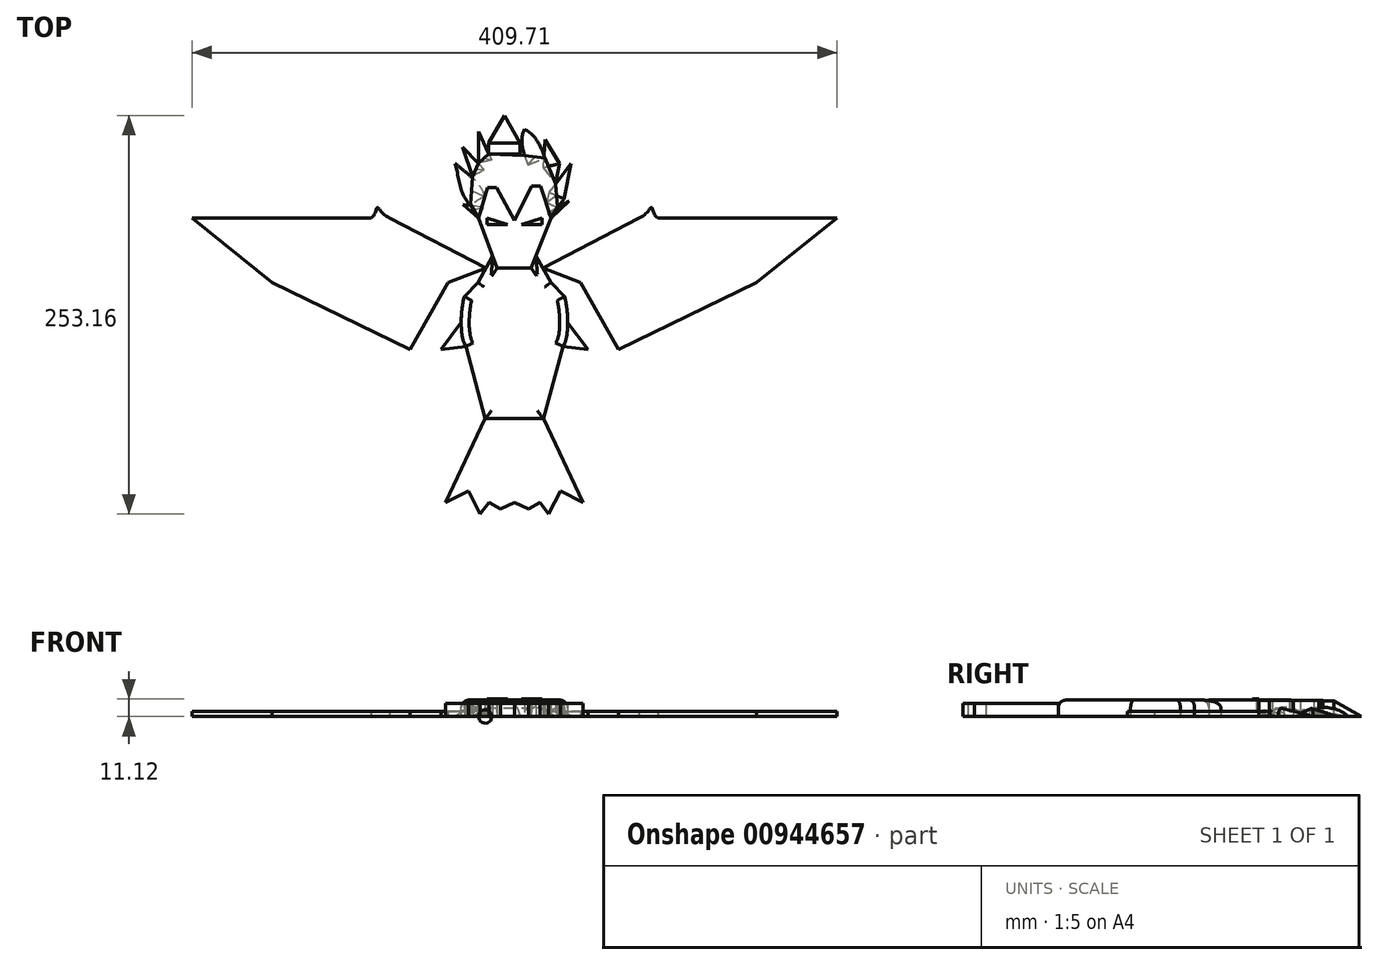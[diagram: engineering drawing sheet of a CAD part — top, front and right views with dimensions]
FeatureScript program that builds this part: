
annotation { "Feature Type Name" : "Feature", "Feature Type Description" : "" }
export const myFeature = defineFeature(function(context is Context, id is Id, definition is map)
    precondition{}
    {
        {
            var Q0;
            Q0=qCreatedBy(makeId("Top.planeOp"),FACE);
            var sketch = newSketch(context, id + "F0", { "sketchPlane" : qUnion([Q0])});
            skLineSegment(sketch, "E0", {"start": v(-66.9, 0) * mm, "end": v(-76.6, 8.61) * mm});
            skLineSegment(sketch, "E1", {"start": v(-76.6, 8.61) * mm, "end": v(-71.81, 8.61) * mm});
            skFitSpline(sketch, "E2", {"points": [v(-71.81, 8.61) * mm, v(-81.52, 34.84) * mm], "startDerivative": vector(-20.15, 14.33) * mm, "endDerivative": vector(-6.58, 25.07) * mm});
            skLineSegment(sketch, "E3", {"start": v(-81.52, 34.84) * mm, "end": v(-70.5, 26.48) * mm});
            skPoint(sketch, "E4.endSnap0", {"position": v(-76.81, 45.33) * mm});
            skLineSegment(sketch, "E5", {"start": v(-66.7, 55.01) * mm, "end": v(-60.24, 40.68) * mm});
            skLineSegment(sketch, "E6", {"start": v(-60.24, 40.68) * mm, "end": v(-60.24, 47.85) * mm});
            skPoint(sketch, "E6.endSnap0", {"position": v(-63.47, 47.85) * mm});
            skLineSegment(sketch, "E7", {"start": v(-60.24, 47.85) * mm, "end": v(-50.37, 65.3) * mm});
            skLineSegment(sketch, "E8", {"start": v(-50.37, 65.3) * mm, "end": v(-45.15, 49.34) * mm});
            skFitSpline(sketch, "E9", {"points": [v(-45.15, 49.34) * mm, v(-37.68, 39.91) * mm], "startDerivative": vector(4.86, -11.5) * mm, "endDerivative": vector(8.7, -8.59) * mm});
            skLineSegment(sketch, "E10", {"start": v(-37.68, 39.91) * mm, "end": v(-37.68, 56.57) * mm});
            skPoint(sketch, "E10.endSnap0", {"position": v(-55.3, 56.57) * mm});
            skFitSpline(sketch, "E11", {"points": [v(-37.68, 56.57) * mm, v(-24.45, 38.08) * mm], "startDerivative": vector(23.87, -11.8) * mm, "endDerivative": vector(8.76, -22.04) * mm});
            skLineSegment(sketch, "E12", {"start": v(-24.45, 38.08) * mm, "end": v(-24.45, 49.93) * mm});
            skLineSegment(sketch, "E13", {"start": v(-24.45, 49.93) * mm, "end": v(-15.46, 34.62) * mm});
            skLineSegment(sketch, "E14", {"start": v(-15.46, 34.62) * mm, "end": v(-17.97, 22.12) * mm});
            skLineSegment(sketch, "E15", {"start": v(-17.97, 22.12) * mm, "end": v(-8.1, 34.62) * mm});
            skLineSegment(sketch, "E16", {"start": v(-8.1, 34.62) * mm, "end": v(-12.58, 12.28) * mm});
            skLineSegment(sketch, "E17", {"start": v(-12.58, 12.28) * mm, "end": v(-16.62, 6.75) * mm});
            skLineSegment(sketch, "E18", {"start": v(-70.5, 26.48) * mm, "end": v(-76.81, 45.33) * mm});
            skLineSegment(sketch, "E19", {"start": v(-66.7, 55.01) * mm, "end": v(-66.7, 35.15) * mm});
            skLineSegment(sketch, "E20", {"start": v(-66.7, 35.15) * mm, "end": v(-76.81, 45.33) * mm});
            skPoint(sketch, "E21.endSnap0", {"position": v(-73.65, 35.9) * mm});
            skLineSegment(sketch, "E22", {"start": v(-43.94, -1.42) * mm, "end": v(-55.3, 19.57) * mm});
            skLineSegment(sketch, "E23", {"start": v(-43.94, -1.42) * mm, "end": v(-33, 20.48) * mm});
            skLineSegment(sketch, "E24", {"start": v(-55.3, 19.57) * mm, "end": v(-60.93, 19.57) * mm});
            skLineSegment(sketch, "E25", {"start": v(-60.93, 19.57) * mm, "end": v(-66.9, 0) * mm});
            skLineSegment(sketch, "E26", {"start": v(-33, 20.48) * mm, "end": v(-27.37, 20.48) * mm});
            skLineSegment(sketch, "E27", {"start": v(-27.37, 20.48) * mm, "end": v(-21.96, 3.92) * mm});
            skLineSegment(sketch, "E28", {"start": v(-21.96, 3.92) * mm, "end": v(-20.68, 0) * mm});
            skLineSegment(sketch, "E29", {"start": v(-16.62, 6.75) * mm, "end": v(-9.22, 10.96) * mm});
            skLineSegment(sketch, "E30", {"start": v(-9.22, 10.96) * mm, "end": v(-20.68, 0) * mm});
            skLineSegment(sketch, "E31", {"start": v(-66.9, 0) * mm, "end": v(-54.89, -31.63) * mm});
            skLineSegment(sketch, "E32", {"start": v(-54.89, -31.63) * mm, "end": v(-43.94, -31.63) * mm});
            skLineSegment(sketch, "E33", {"start": v(-43.94, -31.63) * mm, "end": v(-33.27, -31.63) * mm});
            skLineSegment(sketch, "E34", {"start": v(-33.27, -31.63) * mm, "end": v(-20.68, 0) * mm});
            skLineSegment(sketch, "E35", {"start": v(-43.94, -1.42) * mm, "end": v(-43.94, -31.63) * mm, "construction": true});
            skLineSegment(sketch, "E36", {"start": v(-64.46, -6.43) * mm, "end": v(-22.05, -6.43) * mm, "construction": true});
            skLineSegment(sketch, "E37", {"start": v(-43.94, -1.42) * mm, "end": v(-43.94, 31.12) * mm, "construction": true});
            skLineSegment(sketch, "E38", {"start": v(-30.23, -24) * mm, "end": v(-20.68, -40.76) * mm});
            skLineSegment(sketch, "E39.MirrorCS", {"start": v(-57.66, -24) * mm, "end": v(-64.77, -36.48) * mm});
            skLineSegment(sketch, "E40", {"start": v(-62, -31.63) * mm, "end": v(-74.02, -36.2) * mm});
            skLineSegment(sketch, "E41.MirrorCS", {"start": v(-25.88, -31.63) * mm, "end": v(-1.86, -40.76) * mm});
            skLineSegment(sketch, "E42", {"start": v(-86.03, -40.76) * mm, "end": v(-111.7, -86.16) * mm});
            skLineSegment(sketch, "E43", {"start": v(-43.94, -31.63) * mm, "end": v(-43.94, -131.11) * mm, "construction": true});
            skLineSegment(sketch, "E44.MirrorCS", {"start": v(-1.86, -40.76) * mm, "end": v(37.93, -111.15) * mm});
            skPoint(sketch, "E45.startSnap0", {"position": v(-43.94, -81.37) * mm});
            skLineSegment(sketch, "E46", {"start": v(-43.94, -81.37) * mm, "end": v(-13.98, -81.37) * mm, "construction": true});
            skLineSegment(sketch, "E47", {"start": v(-43.94, -81.37) * mm, "end": v(-74.8, -81.37) * mm, "construction": true});
            skFitSpline(sketch, "E48", {"points": [v(-75.76, -49.7) * mm, v(-74.8, -81.37) * mm], "startDerivative": vector(-6.65, -23.76) * mm, "endDerivative": vector(13.3, -20.9) * mm});
            skFitSpline(sketch, "E49.MirrorCS", {"points": [v(-12.13, -49.7) * mm, v(-13.08, -81.37) * mm], "startDerivative": vector(6.65, -23.76) * mm, "endDerivative": vector(-13.3, -20.9) * mm});
            skLineSegment(sketch, "E50", {"start": v(-74.8, -81.37) * mm, "end": v(-62.45, -127.34) * mm});
            skLineSegment(sketch, "E51.MirrorCS", {"start": v(-13.08, -81.37) * mm, "end": v(-25.43, -127.34) * mm});
            skLineSegment(sketch, "E52", {"start": v(-77.78, -66.16) * mm, "end": v(-115.4, -116.45) * mm});
            skLineSegment(sketch, "E53.MirrorCS", {"start": v(-10.1, -66.16) * mm, "end": v(27.52, -116.45) * mm});
            skLineSegment(sketch, "E54", {"start": v(-49.42, -31.63) * mm, "end": v(-46.5, -45.27) * mm});
            skLineSegment(sketch, "E55.MirrorCS", {"start": v(-38.47, -31.63) * mm, "end": v(-41.39, -45.27) * mm});
            skLineSegment(sketch, "E56", {"start": v(-62.45, -127.34) * mm, "end": v(-25.43, -127.34) * mm});
            skLineSegment(sketch, "E57", {"start": v(-62.45, -127.34) * mm, "end": v(-87.56, -180.45) * mm});
            skLineSegment(sketch, "E58", {"start": v(-43.94, -131.11) * mm, "end": v(-43.94, -225.81) * mm, "construction": true});
            skLineSegment(sketch, "E59", {"start": v(-87.56, -180.45) * mm, "end": v(-73.11, -173.13) * mm});
            skLineSegment(sketch, "E60", {"start": v(-73.11, -173.13) * mm, "end": v(-65.65, -187.87) * mm});
            skLineSegment(sketch, "E61", {"start": v(-65.65, -187.87) * mm, "end": v(-60.1, -180.45) * mm});
            skLineSegment(sketch, "E62", {"start": v(-60.1, -180.45) * mm, "end": v(-52.85, -184.55) * mm});
            skLineSegment(sketch, "E63", {"start": v(-52.85, -184.55) * mm, "end": v(-43.94, -180.45) * mm});
            skLineSegment(sketch, "E64.MirrorCS", {"start": v(-25.43, -127.34) * mm, "end": v(-0.32, -180.45) * mm});
            skLineSegment(sketch, "E65.MirrorCS", {"start": v(-0.32, -180.45) * mm, "end": v(-14.77, -173.13) * mm});
            skLineSegment(sketch, "E66.MirrorCS", {"start": v(-14.77, -173.13) * mm, "end": v(-22.24, -187.87) * mm});
            skLineSegment(sketch, "E67.MirrorCS", {"start": v(-27.8, -180.45) * mm, "end": v(-35.04, -184.55) * mm});
            skLineSegment(sketch, "E68.MirrorCS", {"start": v(-35.04, -184.55) * mm, "end": v(-43.94, -180.45) * mm});
            skLineSegment(sketch, "E69.MirrorCS", {"start": v(-22.24, -187.87) * mm, "end": v(-27.8, -180.45) * mm});
            skPoint(sketch, "E70.1.internal.snap0", {"position": v(-69.38, -180.5) * mm});
            skLineSegment(sketch, "E71", {"start": v(-73.11, -173.13) * mm, "end": v(-113.4, -264.9) * mm});
            skLineSegment(sketch, "E72.MirrorCS", {"start": v(-14.77, -173.13) * mm, "end": v(25.5, -264.9) * mm});
            skLineSegment(sketch, "E73", {"start": v(-35.04, -184.55) * mm, "end": v(9.92, -264.08) * mm});
            skLineSegment(sketch, "E74.MirrorCS", {"start": v(-52.85, -184.55) * mm, "end": v(-97.8, -264.08) * mm});
            skLineSegment(sketch, "E75", {"start": v(-67.2, -40.76) * mm, "end": v(-71.48, -45.22) * mm});
            skLineSegment(sketch, "E76", {"start": v(-20.68, -40.76) * mm, "end": v(-12.13, -49.7) * mm});
            skLineSegment(sketch, "E77", {"start": v(-125.82, -111.15) * mm, "end": v(-115.4, -116.45) * mm});
            skLineSegment(sketch, "E78", {"start": v(27.52, -116.45) * mm, "end": v(37.93, -111.15) * mm});
            skLineSegment(sketch, "E79", {"start": v(9.92, -264.08) * mm, "end": v(25.5, -264.9) * mm});
            skLineSegment(sketch, "E80", {"start": v(-113.4, -264.9) * mm, "end": v(-97.8, -264.08) * mm});
            skLineSegment(sketch, "E81", {"start": v(-115.4, -116.45) * mm, "end": v(-115.4, -116.45) * mm});
            skLineSegment(sketch, "E82", {"start": v(-111.7, -86.16) * mm, "end": v(-125.82, -111.15) * mm});
            skLineSegment(sketch, "E83", {"start": v(-74.02, -36.2) * mm, "end": v(-86.03, -40.76) * mm});
            skLineSegment(sketch, "E84", {"start": v(-71.48, -45.22) * mm, "end": v(-75.76, -49.7) * mm});
            skLineSegment(sketch, "E85", {"start": v(-64.77, -36.48) * mm, "end": v(-67.2, -40.76) * mm});
            skLineSegment(sketch, "E86", {"start": v(-37.68, 39.91) * mm, "end": v(-24.45, 38.08) * mm});
            skLineSegment(sketch, "E87", {"start": v(-24.45, 38.08) * mm, "end": v(-17.97, 22.12) * mm});
            skLineSegment(sketch, "E88", {"start": v(-17.97, 22.12) * mm, "end": v(-16.62, 6.75) * mm});
            skLineSegment(sketch, "E89", {"start": v(-16.62, 6.75) * mm, "end": v(-20.68, 0) * mm});
            skLineSegment(sketch, "E90", {"start": v(-37.68, 39.91) * mm, "end": v(-60.24, 40.68) * mm});
            skLineSegment(sketch, "E91", {"start": v(-60.24, 40.68) * mm, "end": v(-66.7, 35.15) * mm});
            skLineSegment(sketch, "E92", {"start": v(-66.7, 35.15) * mm, "end": v(-70.5, 26.48) * mm});
            skLineSegment(sketch, "E93", {"start": v(-70.5, 26.48) * mm, "end": v(-71.81, 8.61) * mm});
            skLineSegment(sketch, "E94", {"start": v(-71.81, 8.61) * mm, "end": v(-66.9, 0) * mm});
            skLineSegment(sketch, "E95", {"start": v(-81.52, 34.84) * mm, "end": v(-71.15, 17.55) * mm});
            skLineSegment(sketch, "E96", {"start": v(-76.81, 45.33) * mm, "end": v(-68.4, 31.28) * mm});
            skLineSegment(sketch, "E97", {"start": v(-66.7, 55.01) * mm, "end": v(-63.02, 38.3) * mm});
            skLineSegment(sketch, "E98", {"start": v(-24.45, 49.93) * mm, "end": v(-17.97, 22.12) * mm});
            skLineSegment(sketch, "E99", {"start": v(-8.1, 34.62) * mm, "end": v(-17.3, 14.43) * mm});
            skLineSegment(sketch, "E100", {"start": v(-9.22, 10.96) * mm, "end": v(-18.07, 4.33) * mm});
            skLineSegment(sketch, "E101", {"start": v(-50.37, 65.3) * mm, "end": v(-50.37, 40.35) * mm});
            skLineSegment(sketch, "E102", {"start": v(-37.68, 56.57) * mm, "end": v(-31.07, 39) * mm});
            skLineSegment(sketch, "E103", {"start": v(-76.6, 8.61) * mm, "end": v(-70.13, 5.66) * mm});
            skLineSegment(sketch, "E104", {"start": v(-25.88, -31.63) * mm, "end": v(35.22, 0) * mm});
            skLineSegment(sketch, "E105", {"start": v(35.22, 0) * mm, "end": v(160.91, 0) * mm});
            skLineSegment(sketch, "E106", {"start": v(160.91, 0) * mm, "end": v(109.93, -40.76) * mm});
            skLineSegment(sketch, "E107.MirrorCS", {"start": v(-123.1, 0) * mm, "end": v(-248.8, 0) * mm});
            skLineSegment(sketch, "E108.MirrorCS", {"start": v(-62, -31.63) * mm, "end": v(-123.1, 0) * mm});
            skLineSegment(sketch, "E109.MirrorCS", {"start": v(-248.8, 0) * mm, "end": v(-197.82, -40.76) * mm});
            skLineSegment(sketch, "E110", {"start": v(109.93, -40.76) * mm, "end": v(22.27, -83.44) * mm});
            skLineSegment(sketch, "E111.MirrorCS", {"start": v(-197.82, -40.76) * mm, "end": v(-110.15, -83.44) * mm});
            skLineSegment(sketch, "E112", {"start": v(-90.7, -83.44) * mm, "end": v(-74.8, -81.37) * mm});
            skLineSegment(sketch, "E113.MirrorCS", {"start": v(2.82, -83.44) * mm, "end": v(-13.08, -81.37) * mm});
            skFitSpline(sketch, "E114", {"points": [v(35.22, 0) * mm, v(43.15, 6.85) * mm, v(47.2, 0) * mm], "startDerivative": vector(30.5, 14.02) * mm, "endDerivative": vector(21.86, -16.08) * mm});
            skFitSpline(sketch, "E115.MirrorCS", {"points": [v(-123.1, 0) * mm, v(-131.03, 6.85) * mm, v(-135.1, 0) * mm], "startDerivative": vector(-30.5, 14.02) * mm, "endDerivative": vector(-21.86, -16.08) * mm});
            skSolve(sketch);
        }
        {
            var Q0;
            {var subQ0=sQuery(id+"F0.wireOp",EDGE,"E2");Q0=makeQuery(id+"F0.imprint","IMPRINT",FACE,{"disambiguationData":[TD([[makeQuery(id+"F0.imprint","IMPRINT",EDGE,{"derivedFrom":subQ0}),-1.0]])]});}
            var Q1;
            Q1=sQuery(id+"F0.wireOp",EDGE,"E95");
            revolve(context, id + "F1", {"surfaceOperationType" : NewSurfaceOperationType.NEW, "entities" : qUnion([Q0]), "axis" : qUnion([Q1]), "revolveType" : RevolveType.ONE_DIRECTION, "oppositeDirection" : true, "angle" : 180 * degree});
        }
        {
            var Q0;
            {var subQ0=sQuery(id+"F0.wireOp",EDGE,"E18");Q0=makeQuery(id+"F0.imprint","IMPRINT",FACE,{"disambiguationData":[TD([[makeQuery(id+"F0.imprint","IMPRINT",EDGE,{"derivedFrom":subQ0}),-1.0]])]});}
            var Q1;
            Q1=sQuery(id+"F0.wireOp",EDGE,"E96");
            revolve(context, id + "F2", {"surfaceOperationType" : NewSurfaceOperationType.NEW, "entities" : qUnion([Q0]), "axis" : qUnion([Q1]), "revolveType" : RevolveType.ONE_DIRECTION, "oppositeDirection" : true, "angle" : 180 * degree});
        }
        {
            var Q0;
            {var subQ0=sQuery(id+"F0.wireOp",EDGE,"E19");Q0=makeQuery(id+"F0.imprint","IMPRINT",FACE,{"disambiguationData":[TD([[makeQuery(id+"F0.imprint","IMPRINT",EDGE,{"derivedFrom":subQ0}),1.0]])]});}
            var Q1;
            Q1=sQuery(id+"F0.wireOp",EDGE,"E97");
            revolve(context, id + "F3", {"surfaceOperationType" : NewSurfaceOperationType.NEW, "entities" : qUnion([Q0]), "axis" : qUnion([Q1]), "revolveType" : RevolveType.ONE_DIRECTION, "oppositeDirection" : true, "angle" : 180 * degree});
        }
        {
            var Q0;
            Q0=makeQuery(id+"F0.imprint","IMPRINT",FACE,{"disambiguationData":[TD([[makeQuery(id+"F0.imprint","IMPRINT",EDGE,{"derivedFrom":sQuery(id+"F0.wireOp",EDGE,"E13")}),-1.0]])]});
            var Q1;
            Q1=sQuery(id+"F0.wireOp",EDGE,"E98");
            revolve(context, id + "F4", {"surfaceOperationType" : NewSurfaceOperationType.NEW, "entities" : qUnion([Q0]), "axis" : qUnion([Q1]), "revolveType" : RevolveType.ONE_DIRECTION, "angle" : 180 * degree});
        }
        {
            var Q0;
            Q0=makeQuery(id+"F0.imprint","IMPRINT",FACE,{"disambiguationData":[TD([[makeQuery(id+"F0.imprint","IMPRINT",EDGE,{"derivedFrom":sQuery(id+"F0.wireOp",EDGE,"E16")}),-1.0]])]});
            var Q1;
            Q1=sQuery(id+"F0.wireOp",EDGE,"E99");
            revolve(context, id + "F5", {"surfaceOperationType" : NewSurfaceOperationType.NEW, "entities" : qUnion([Q0]), "axis" : qUnion([Q1]), "revolveType" : RevolveType.ONE_DIRECTION, "angle" : 180 * degree});
        }
        {
            var Q0;
            {var subQ0=sQuery(id+"F0.wireOp",EDGE,"E30");Q0=makeQuery(id+"F0.imprint","IMPRINT",FACE,{"disambiguationData":[TD([[makeQuery(id+"F0.imprint","IMPRINT",EDGE,{"derivedFrom":subQ0}),-1.0]])]});}
            var Q1;
            Q1=sQuery(id+"F0.wireOp",EDGE,"E100");
            revolve(context, id + "F6", {"surfaceOperationType" : NewSurfaceOperationType.NEW, "entities" : qUnion([Q0]), "axis" : qUnion([Q1]), "revolveType" : RevolveType.ONE_DIRECTION, "angle" : 180 * degree});
        }
        {
            var Q0;
            {var subQ0=sQuery(id+"F0.wireOp",EDGE,"E11");Q0=makeQuery(id+"F0.imprint","IMPRINT",FACE,{"disambiguationData":[TD([[makeQuery(id+"F0.imprint","IMPRINT",EDGE,{"derivedFrom":subQ0}),-1.0]])]});}
            var Q1;
            Q1=sQuery(id+"F0.wireOp",EDGE,"E102");
            revolve(context, id + "F7", {"operationType" : NewBodyOperationType.ADD, "surfaceOperationType" : NewSurfaceOperationType.NEW, "entities" : qUnion([Q0]), "axis" : qUnion([Q1]), "revolveType" : RevolveType.ONE_DIRECTION, "angle" : 180 * degree});
        }
        {
            var Q0;
            {var subQ0=sQuery(id+"F0.wireOp",EDGE,"E6");Q0=makeQuery(id+"F0.imprint","IMPRINT",FACE,{"disambiguationData":[TD([[makeQuery(id+"F0.imprint","IMPRINT",EDGE,{"derivedFrom":subQ0}),-1.0]])]});}
            var Q1;
            Q1=sQuery(id+"F0.wireOp",EDGE,"E101");
            revolve(context, id + "F8", {"operationType" : NewBodyOperationType.ADD, "surfaceOperationType" : NewSurfaceOperationType.NEW, "entities" : qUnion([Q0]), "axis" : qUnion([Q1]), "revolveType" : RevolveType.ONE_DIRECTION, "oppositeDirection" : true, "angle" : 180 * degree});
        }
        {
            var Q0;
            {var subQ0=sQuery(id+"F0.wireOp",EDGE,"E0");Q0=makeQuery(id+"F0.imprint","IMPRINT",FACE,{"disambiguationData":[TD([[makeQuery(id+"F0.imprint","IMPRINT",EDGE,{"derivedFrom":subQ0}),-1.0]])]});}
            var Q1;
            Q1=sQuery(id+"F0.wireOp",EDGE,"E103");
            revolve(context, id + "F9", {"surfaceOperationType" : NewSurfaceOperationType.NEW, "entities" : qUnion([Q0]), "axis" : qUnion([Q1]), "revolveType" : RevolveType.ONE_DIRECTION, "oppositeDirection" : true, "angle" : 180 * degree});
        }
        {
            var Q0;
            Q0=makeQuery(id+"F0.imprint","IMPRINT",FACE,{"disambiguationData":[TD([[makeQuery(id+"F0.imprint","IMPRINT",EDGE,{"derivedFrom":sQuery(id+"F0.wireOp",EDGE,"E22")}),-1.0]])]});
            extrude(context, id + "F10", {"entities" : qUnion([Q0]), "depth" : 10.16 * mm, "offsetDistance" : 25.4 * mm});
        }
        {
            var Q0;
            {var subQ20=sQuery(id+"F0.wireOp",EDGE,"E50");Q0=makeQuery(id+"F0.imprint","IMPRINT",FACE,{"disambiguationData":[TD([[makeQuery(id+"F0.imprint","IMPRINT",EDGE,{"derivedFrom":subQ20}),1.0]])]});}
            extrude(context, id + "F11", {"entities" : qUnion([Q0]), "depth" : 10.4 * mm, "offsetDistance" : 25.4 * mm});
        }
        {
            var Q0;
            Q0=makeQuery(id+"F11.opExtrude","CAP_FACE",FACE,{"disambiguationData":[OSD([sQuery(id+"F0.wireOp",EDGE,"E31"),sQuery(id+"F0.wireOp",EDGE,"E32"),sQuery(id+"F0.wireOp",EDGE,"E33"),sQuery(id+"F0.wireOp",EDGE,"E34"),sQuery(id+"F0.wireOp",EDGE,"E38"),sQuery(id+"F0.wireOp",EDGE,"E39.MirrorCS"),sQuery(id+"F0.wireOp",EDGE,"E48"),sQuery(id+"F0.wireOp",EDGE,"E49.MirrorCS"),sQuery(id+"F0.wireOp",EDGE,"E50"),sQuery(id+"F0.wireOp",EDGE,"E51.MirrorCS"),sQuery(id+"F0.wireOp",EDGE,"E56"),sQuery(id+"F0.wireOp",EDGE,"E75"),sQuery(id+"F0.wireOp",EDGE,"E76"),sQuery(id+"F0.wireOp",EDGE,"E84"),sQuery(id+"F0.wireOp",EDGE,"E85")])],"isStart":false});
            fillet(context, id + "F12", {"entities" : qUnion([Q0]), "radius" : 5.08 * mm, "tangentPropagation" : true, "allowEdgeOverflow" : false});
        }
        {
            var Q0;
            Q0=makeQuery(id+"F0.imprint","IMPRINT",FACE,{"disambiguationData":[TD([[makeQuery(id+"F0.imprint","IMPRINT",EDGE,{"derivedFrom":sQuery(id+"F0.wireOp",EDGE,"E40")}),-1.0]])]});
            var Q1;
            {var subQ1=sQuery(id+"F0.wireOp",EDGE,"E41.MirrorCS");Q1=makeQuery(id+"F0.imprint","IMPRINT",FACE,{"disambiguationData":[TD([[makeQuery(id+"F0.imprint","IMPRINT",EDGE,{"derivedFrom":subQ1}),1.0]])]});}
            var Q2;
            {var subQ0=sQuery(id+"F0.wireOp",EDGE,"E113.MirrorCS");Q2=makeQuery(id+"F0.imprint","IMPRINT",FACE,{"disambiguationData":[TD([[makeQuery(id+"F0.imprint","IMPRINT",EDGE,{"derivedFrom":subQ0}),-1.0]])]});}
            var Q3;
            {var subQ0=sQuery(id+"F0.wireOp",EDGE,"E112");Q3=makeQuery(id+"F0.imprint","IMPRINT",FACE,{"disambiguationData":[TD([[makeQuery(id+"F0.imprint","IMPRINT",EDGE,{"derivedFrom":subQ0}),1.0]])]});}
            var Q4;
            {var subQ0=sQuery(id+"F0.wireOp",EDGE,"E115.MirrorCS");Q4=makeQuery(id+"F0.imprint","IMPRINT",FACE,{"disambiguationData":[TD([[makeQuery(id+"F0.imprint","IMPRINT",EDGE,{"derivedFrom":subQ0}),1.0]])]});}
            var Q5;
            {var subQ0=sQuery(id+"F0.wireOp",EDGE,"E114");Q5=makeQuery(id+"F0.imprint","IMPRINT",FACE,{"disambiguationData":[TD([[makeQuery(id+"F0.imprint","IMPRINT",EDGE,{"derivedFrom":subQ0}),-1.0]])]});}
            extrude(context, id + "F13", {"entities" : qUnion([Q0, Q1, Q2, Q3, Q4, Q5]), "depth" : 3.3 * mm, "offsetDistance" : 25.4 * mm});
        }
        {
            var Q0;
            {var subQ9=sQuery(id+"F0.wireOp",EDGE,"E40");Q0=makeQuery(id+"F0.imprint","IMPRINT",FACE,{"disambiguationData":[TD([[makeQuery(id+"F0.imprint","IMPRINT",EDGE,{"derivedFrom":subQ9}),1.0]])]});}
            extrude(context, id + "F14", {"entities" : qUnion([Q0]), "depth" : 10.4 * mm, "offsetDistance" : 25.4 * mm});
        }
        {
            var Q0;
            Q0=makeQuery(id+"F14.opExtrude","SWEPT_BODY",BODY,{"disambiguationData":[OSD([sQuery(id+"F0.wireOp",EDGE,"E39.MirrorCS"),sQuery(id+"F0.wireOp",EDGE,"E40"),sQuery(id+"F0.wireOp",EDGE,"E42"),sQuery(id+"F0.wireOp",EDGE,"E48"),sQuery(id+"F0.wireOp",EDGE,"E52"),sQuery(id+"F0.wireOp",EDGE,"E75"),sQuery(id+"F0.wireOp",EDGE,"E77"),sQuery(id+"F0.wireOp",EDGE,"E82"),sQuery(id+"F0.wireOp",EDGE,"E83"),sQuery(id+"F0.wireOp",EDGE,"E84"),sQuery(id+"F0.wireOp",EDGE,"E85")])]});
            deleteBodies(context, id + "F15", {"entities" : qUnion([Q0])});
        }
        {
            var Q0;
            Q0=makeQuery(id+"F0.imprint","IMPRINT",FACE,{"disambiguationData":[TD([[makeQuery(id+"F0.imprint","IMPRINT",EDGE,{"derivedFrom":sQuery(id+"F0.wireOp",EDGE,"E22")}),1.0]])]});
            extrude(context, id + "F16", {"entities" : qUnion([Q0]), "depth" : 10.62 * mm, "offsetDistance" : 25.4 * mm});
        }
        {
            var Q0;
            Q0=makeQuery(id+"F0.imprint","IMPRINT",FACE,{"disambiguationData":[TD([[makeQuery(id+"F0.imprint","IMPRINT",EDGE,{"derivedFrom":sQuery(id+"F0.wireOp",EDGE,"E56")}),-1.0]])]});
            extrude(context, id + "F17", {"entities" : qUnion([Q0]), "operationType" : NewBodyOperationType.ADD, "depth" : 8.38 * mm, "offsetDistance" : 25.4 * mm});
        }
        {
            var Q0;
            Q0=makeQuery(id+"F16.opExtrude","CAP_FACE",FACE,{"disambiguationData":[OSD([sQuery(id+"F0.wireOp",EDGE,"E22"),sQuery(id+"F0.wireOp",EDGE,"E23"),sQuery(id+"F0.wireOp",EDGE,"E24"),sQuery(id+"F0.wireOp",EDGE,"E25"),sQuery(id+"F0.wireOp",EDGE,"E26"),sQuery(id+"F0.wireOp",EDGE,"E27"),sQuery(id+"F0.wireOp",EDGE,"E28"),sQuery(id+"F0.wireOp",EDGE,"E31"),sQuery(id+"F0.wireOp",EDGE,"E32"),sQuery(id+"F0.wireOp",EDGE,"E33"),sQuery(id+"F0.wireOp",EDGE,"E34")])],"isStart":false});
            var sketch = newSketch(context, id + "F18", { "sketchPlane" : qUnion([Q0])});
            skLineSegment(sketch, "E116", {"start": v(-61.46, 0) * mm, "end": v(-61.46, -4.07) * mm});
            skLineSegment(sketch, "E117", {"start": v(-61.46, -4.07) * mm, "end": v(-48.32, -4.07) * mm});
            skLineSegment(sketch, "E118", {"start": v(-48.32, -4.07) * mm, "end": v(-61.46, 0) * mm});
            skLineSegment(sketch, "E119.MirrorCS", {"start": v(-39.57, -4.07) * mm, "end": v(-26.43, 0) * mm});
            skLineSegment(sketch, "E120.MirrorCS", {"start": v(-26.43, -4.07) * mm, "end": v(-39.57, -4.07) * mm});
            skLineSegment(sketch, "E121.MirrorCS", {"start": v(-26.43, 0) * mm, "end": v(-26.43, -4.07) * mm});
            skFitSpline(sketch, "E122", {"points": [v(-52.92, -14.04) * mm, v(-39.65, -11.8) * mm, v(-34.76, -15.92) * mm], "startDerivative": vector(-8.38, 15.93) * mm, "endDerivative": vector(-3.32, 12.44) * mm});
            skSolve(sketch);
        }
        {
            var Q0;
            Q0=makeQuery(id+"F18.imprint","IMPRINT",FACE,{"disambiguationData":[TD([[makeQuery(id+"F18.imprint","IMPRINT",EDGE,{"derivedFrom":sQuery(id+"F18.wireOp",EDGE,"E116")}),1.0]])]});
            var Q1;
            Q1=makeQuery(id+"F18.imprint","IMPRINT",FACE,{"disambiguationData":[TD([[makeQuery(id+"F18.imprint","IMPRINT",EDGE,{"derivedFrom":sQuery(id+"F18.wireOp",EDGE,"E119.MirrorCS")}),-1.0]])]});
            extrude(context, id + "F19", {"entities" : qUnion([Q0, Q1]), "operationType" : NewBodyOperationType.ADD, "depth" : .5 * mm, "offsetDistance" : 25.4 * mm});
        }
    });
